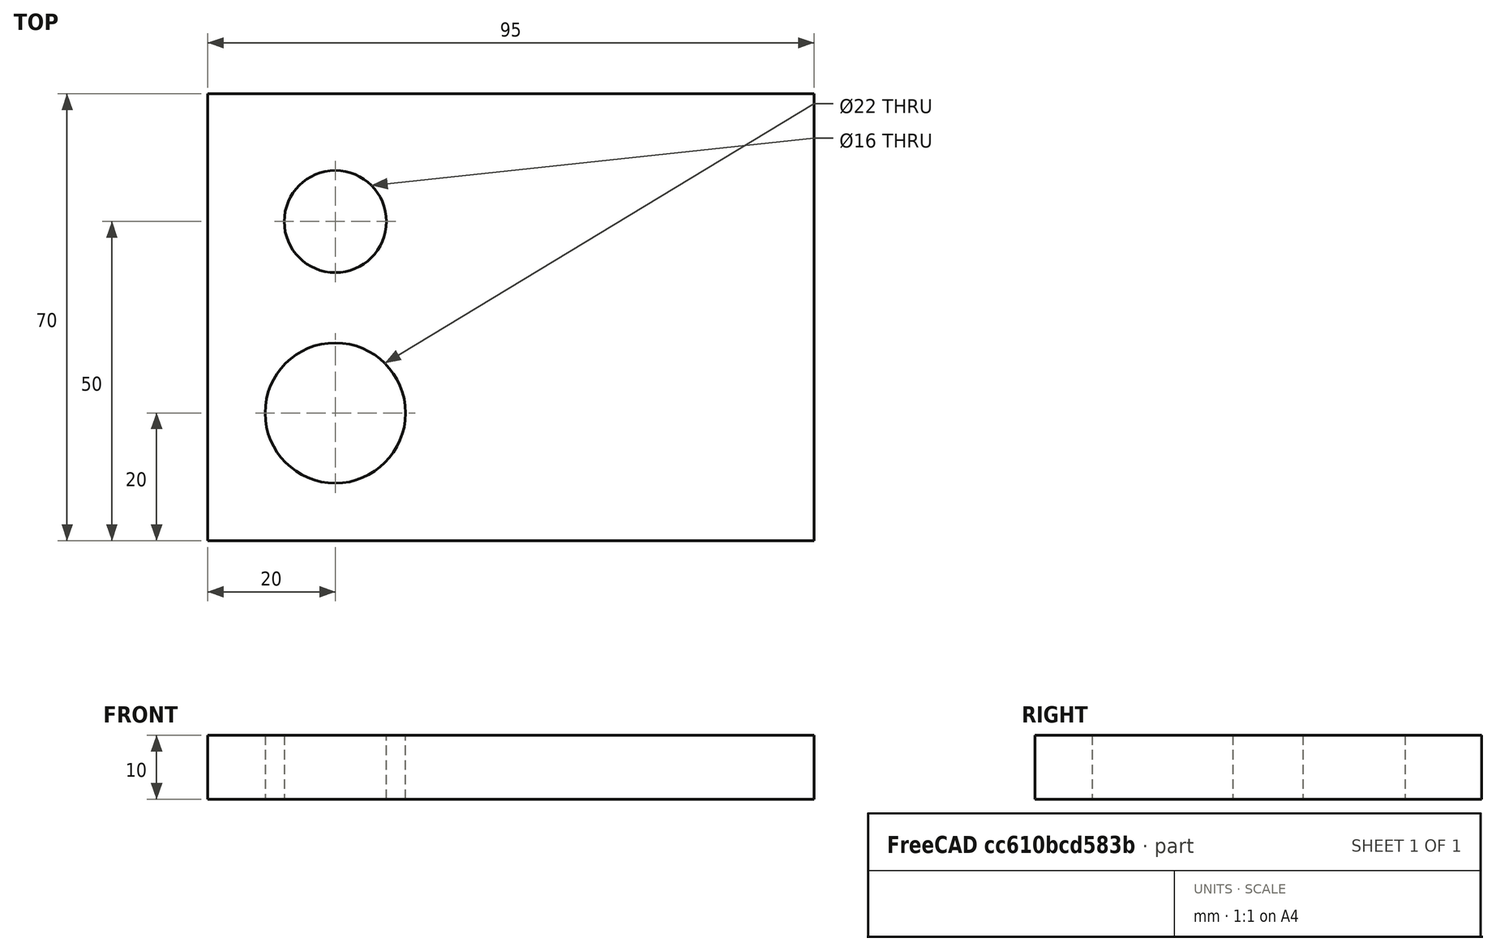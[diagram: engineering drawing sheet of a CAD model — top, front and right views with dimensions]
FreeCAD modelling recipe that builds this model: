
FCSTD DOCUMENT  (FreeCAD 0.19R24276 (Git))
Label: BLDC_holder_ass
License: All rights reserved
LicenseURL: http://en.wikipedia.org/wiki/All_rights_reserved
objects: Sketcher::SketchObject×1, PartDesign::Pad×1, PartDesign::Body×1
note: 4 computed .brp shape members not serialized (recipe doc carries the construction recipe); baked Part::Feature solids carry a one-line shape summary decoded from their .brp

FEATURE [Sketcher::SketchObject] Sketch
  FullyConstrained = true
  MapMode = 5
  Support = -> [XY_Plane]
  sketch-geometry (6):
    g0: Circle CenterX=0 CenterY=0 CenterZ=0 NormalX=0 NormalY=0 NormalZ=1 AngleXU=0 Radius=8
    g1: Circle CenterX=0 CenterY=-30 CenterZ=0 NormalX=0 NormalY=0 NormalZ=1 AngleXU=0 Radius=11
    g2: LineSegment StartX=-20 StartY=20 StartZ=0 EndX=75 EndY=20 EndZ=0
    g3: LineSegment StartX=75 StartY=20 StartZ=0 EndX=75 EndY=-50 EndZ=0
    g4: LineSegment StartX=75 StartY=-50 StartZ=0 EndX=-20 EndY=-50 EndZ=0
    g5: LineSegment StartX=-20 StartY=-50 StartZ=0 EndX=-20 EndY=20 EndZ=0
  constraints (17):
    c: Coincident(g0,g-1)
    c: Diameter(g0) = 16
    c: PointOnObject(g1,g-2)
    c: Diameter(g1) = 22
    c: DistanceY(g1,g0) = 30
    c: Coincident(g2,g3)
    c: Coincident(g3,g4)
    c: Coincident(g4,g5)
    c: Coincident(g5,g2)
    c: Horizontal(g2)
    c: Horizontal(g4)
    c: Vertical(g3)
    c: Vertical(g5)
    c: DistanceX(g0,g2) = 75
    c: DistanceY(g0,g2) = 20
    c: DistanceY(g4,g1) = 20
    c: DistanceX(g2,g0) = 20
FEATURE [PartDesign::Pad] Pad
  Direction = (1,1,1)
  Length = 10
  Length2 = 100
  Profile = -> Sketch
  Type = 0
FEATURE [PartDesign::Body] Body
  Group = -> [Sketch,Pad]
  Origin = -> Origin
  Tip = -> Pad
